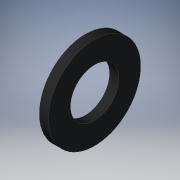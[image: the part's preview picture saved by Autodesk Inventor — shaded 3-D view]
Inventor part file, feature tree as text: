
AUTODESK INVENTOR PART (.ipt)
format: ipt  version: 2019 (Build 230136000, 136)  size: 113,664 bytes
history: native  units: mm
features: other x7, extrude x1, sketch x1
ambient origin geometry x8: Origin, YZ Plane, XZ Plane, XY Plane, X Axis, Y Axis, Z Axis, Center Point
bodies: Solid1 (feature_tree)
feature tree (9):
  extrude  "Extrusion1"  TaperAngle=0.0deg  [1 undecoded]
  other  "BLS_1_XY"
  other  "BLS_1_YZ"
  other  "BLS_1_ZX"
  other  "BLS_1_X"
  other  "BLS_1_Y"
  other  "BLS_1_Z"
  other  "BLS_1_Center"
  sketch  "Skizze_1"  dims[d0=1.6mm d1=0.0mm d2=0.0mm]
note: 1 required parameter value undecoded (feature->parameter linkage not recoverable at this tier; creation-order binding heuristic only, values carry confidence <= 0.55)
